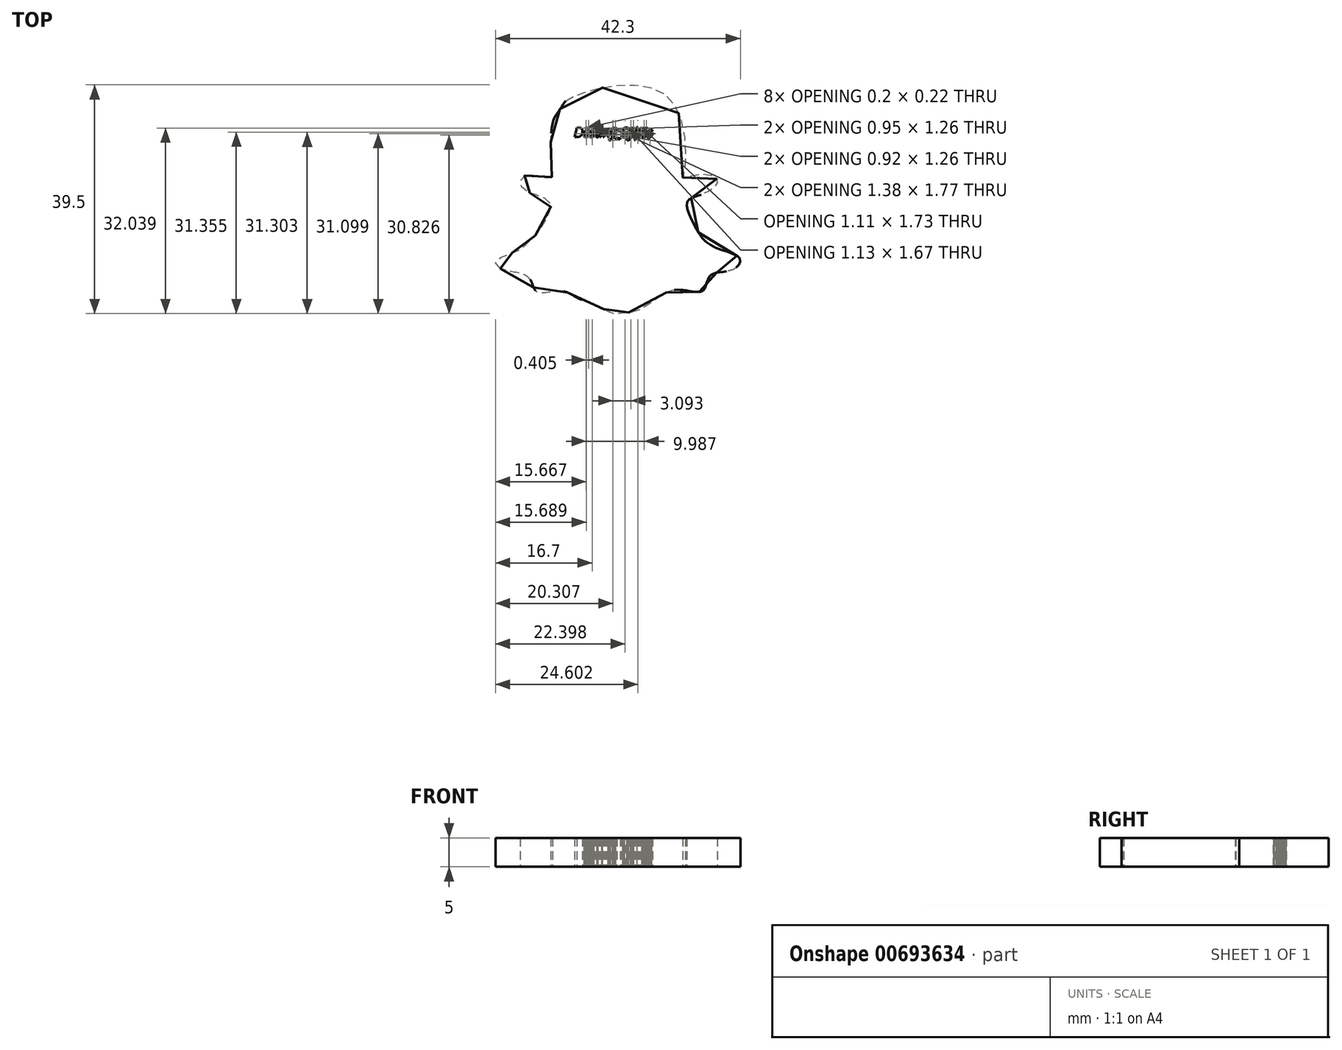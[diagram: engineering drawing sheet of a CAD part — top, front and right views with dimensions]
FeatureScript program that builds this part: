
annotation { "Feature Type Name" : "Feature", "Feature Type Description" : "" }
export const myFeature = defineFeature(function(context is Context, id is Id, definition is map)
    precondition{}
    {
        {
            var Q0;
            Q0=qCreatedBy(makeId("Top.planeOp"),FACE);
            var sketch = newSketch(context, id + "F0", { "sketchPlane" : qUnion([Q0])});
            skFitSpline(sketch, "E0", {"points": [v(-19.35, -10.68) * mm, v(-20.19, -9.5) * mm, v(-18.26, -8.3) * mm, v(-16.18, -7.45) * mm, v(-14.46, -6.05) * mm, v(-12.5, -3.9) * mm, v(-10.99, -1.05) * mm, v(-10.76, 0.59) * mm, v(-12.31, 1.76) * mm, v(-14.33, 2.41) * mm, v(-15.71, 3.44) * mm, v(-15.91, 4.56) * mm, v(-14.85, 5.54) * mm, v(-13.2, 5.36) * mm, v(-10.6, 5.08) * mm, v(-10.6, 7.74) * mm, v(-10.66, 11.34) * mm, v(-10.16, 15.08) * mm, v(-8.84, 17.18) * mm, v(-7.45, 18.68) * mm, v(9.42, 19.1) * mm, v(12.2, 5.35) * mm, v(12.13, 5.07) * mm, v(16.1, 5.63) * mm, v(18.08, 4.42) * mm, v(15.97, 2.36) * mm, v(12.93, 0.96) * mm, v(13.92, -2.78) * mm, v(17.1, -6.7) * mm, v(21.98, -8.95) * mm, v(20.8, -10.82) * mm, v(17.03, -11.75) * mm, v(16.03, -13.8) * mm, v(15.18, -14.65) * mm, v(12.13, -14.37) * mm, v(9.23, -14.84) * mm, v(4.67, -17.74) * mm, v(1.43, -18.39) * mm, v(0, -18.39) * mm, v(-1.61, -17.64) * mm, v(-5.97, -15.77) * mm, v(-8.95, -14.56) * mm, v(-13.11, -14.65) * mm, v(-14.5, -12.22) * mm, v(-19.35, -10.68) * mm]});
            skText(sketch, "E1", { "text": "Dëstinÿ_Sÿkës", "fontName": "OpenSans-Italic.ttf"});
            const initialGuessF0  = {"E1": [-0.00664, 0.01204, 1, 0, 0.00164]};
            skSetInitialGuess(sketch, initialGuessF0);
            skSolve(sketch);
        }
        {
            var Q0;
            Q0 = qSketchRegion(id + "F0", true);
            extrude(context, id + "F1", {"entities" : qUnion([Q0]), "depth" : 5 * mm, "offsetDistance" : 25.4 * mm});
        }
    });
